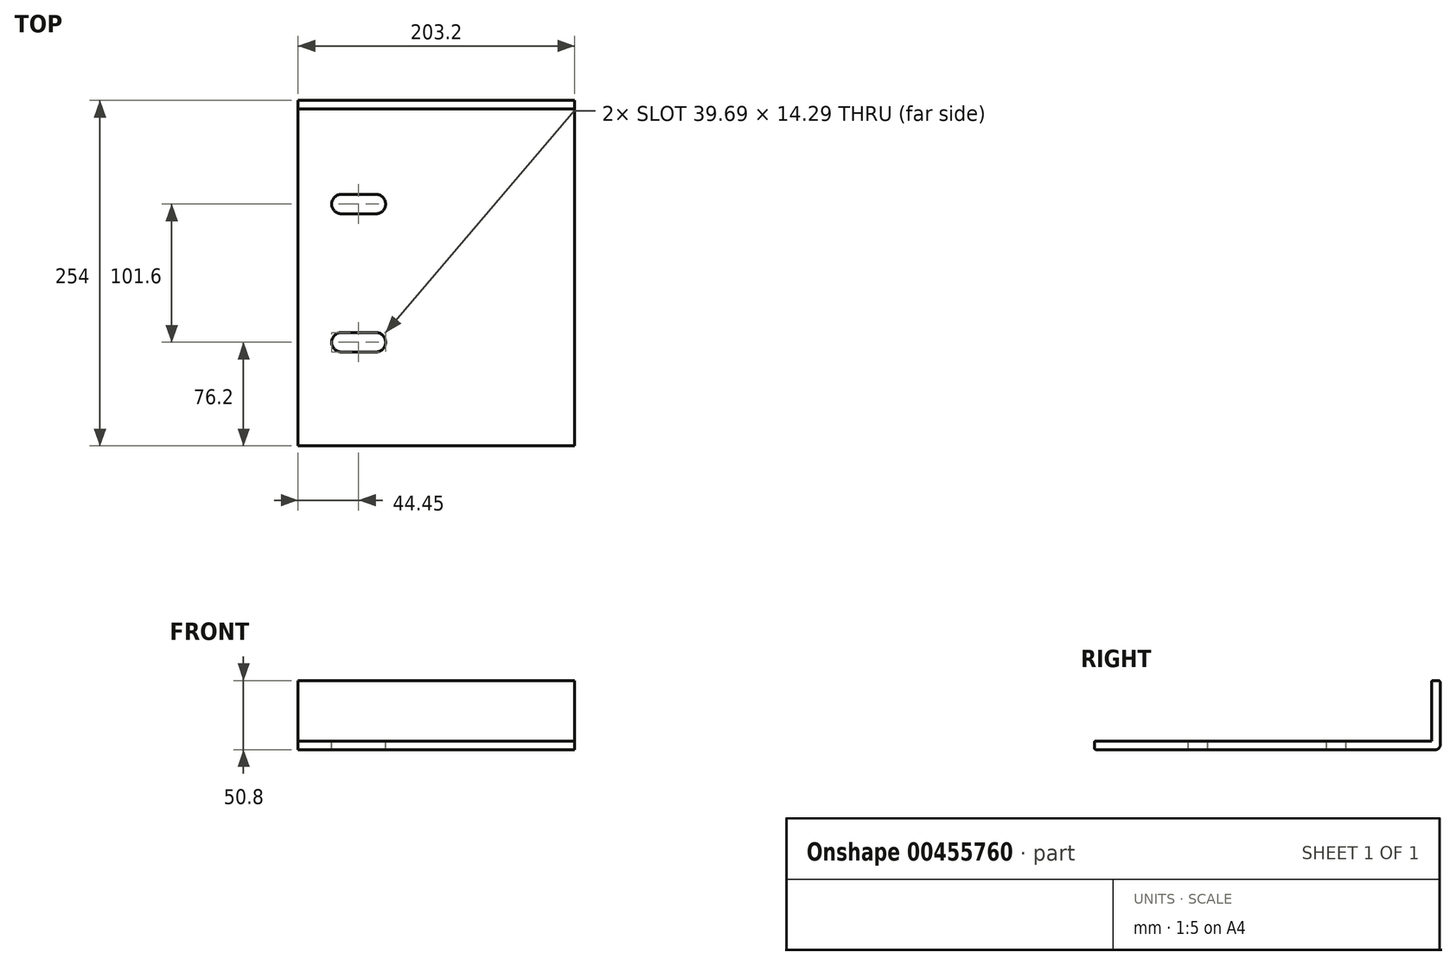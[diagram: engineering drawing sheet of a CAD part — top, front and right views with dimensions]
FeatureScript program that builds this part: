
annotation { "Feature Type Name" : "Feature", "Feature Type Description" : "" }
export const myFeature = defineFeature(function(context is Context, id is Id, definition is map)
    precondition{}
    {
        {
            var Q0;
            Q0=qCreatedBy(makeId("Top.planeOp"),FACE);
            var sketch = newSketch(context, id + "F0", { "sketchPlane" : qUnion([Q0])});
            skLineSegment(sketch, "E0.bottom", {"start": v(-101.6, -127) * mm, "end": v(101.6, -127) * mm});
            skLineSegment(sketch, "E0.top", {"start": v(-101.6, 127) * mm, "end": v(101.6, 127) * mm});
            skLineSegment(sketch, "E0.left", {"start": v(-101.6, -127) * mm, "end": v(-101.6, 127) * mm});
            skLineSegment(sketch, "E0.right", {"start": v(101.6, -127) * mm, "end": v(101.6, 127) * mm});
            skPoint(sketch, "E0.middle", {"position": v(0, 0) * mm});
            skSolve(sketch);
        }
        {
            var Q0;
            Q0 = qSketchRegion(id + "F0", true);
            extrude(context, id + "F1", {"entities" : qUnion([Q0]), "depth" : 6.35 * mm});
        }
        {
            var Q0;
            Q0=makeQuery(id+"F1.opExtrude","CAP_FACE",FACE,{"disambiguationData":[OSD([sQuery(id+"F0.wireOp",EDGE,"E0.bottom"),sQuery(id+"F0.wireOp",EDGE,"E0.top"),sQuery(id+"F0.wireOp",EDGE,"E0.left"),sQuery(id+"F0.wireOp",EDGE,"E0.right")])],"isStart":false});
            var sketch = newSketch(context, id + "F2", { "sketchPlane" : qUnion([Q0])});
            skLineSegment(sketch, "E1.bottom", {"start": v(-101.6, 127) * mm, "end": v(101.6, 127) * mm});
            skLineSegment(sketch, "E1.top", {"start": v(-101.6, 120.65) * mm, "end": v(101.6, 120.65) * mm});
            skLineSegment(sketch, "E1.left", {"start": v(-101.6, 127) * mm, "end": v(-101.6, 120.65) * mm});
            skLineSegment(sketch, "E1.right", {"start": v(101.6, 127) * mm, "end": v(101.6, 120.65) * mm});
            skSolve(sketch);
        }
        {
            var Q0;
            Q0 = qSketchRegion(id + "F2", true);
            extrude(context, id + "F3", {"entities" : qUnion([Q0]), "operationType" : NewBodyOperationType.ADD, "depth" : 44.45 * mm});
        }
        {
            var Q0;
            Q0=makeQuery(id+"F3.opExtrude","CAP_EDGE",EDGE,{"disambiguationData":[OSD([sQuery(id+"F2.wireOp",EDGE,"E1.top")])],"isStart":true});
            var Q1;
            Q1=makeQuery(id+"F1.opExtrude","CAP_EDGE",EDGE,{"disambiguationData":[OSD([sQuery(id+"F0.wireOp",EDGE,"E0.top")])],"isStart":true});
            fillet(context, id + "F4", {"entities" : qUnion([Q0, Q1]), "radius" : 3.17 * mm, "tangentPropagation" : true, "allowEdgeOverflow" : false});
        }
        {
            var Q0;
            Q0=makeQuery(id+"F1.opExtrude","CAP_FACE",FACE,{"disambiguationData":[OSD([sQuery(id+"F0.wireOp",EDGE,"E0.bottom"),sQuery(id+"F0.wireOp",EDGE,"E0.top"),sQuery(id+"F0.wireOp",EDGE,"E0.left"),sQuery(id+"F0.wireOp",EDGE,"E0.right")])],"isStart":false});
            var sketch = newSketch(context, id + "F5", { "sketchPlane" : qUnion([Q0])});
            skLineSegment(sketch, "E2", {"start": v(-101.6, -127) * mm, "end": v(-69.85, -127) * mm, "construction": true});
            skLineSegment(sketch, "E3", {"start": v(-69.85, -127) * mm, "end": v(-69.85, -50.8) * mm, "construction": true});
            skLineSegment(sketch, "E4", {"start": v(-69.85, -50.8) * mm, "end": v(-69.85, 50.8) * mm, "construction": true});
            skLineSegment(sketch, "E5", {"start": v(-69.85, 50.8) * mm, "end": v(-101.6, 50.8) * mm, "construction": true});
            skLineSegment(sketch, "E6", {"start": v(-69.85, -50.8) * mm, "end": v(-101.6, -50.8) * mm, "construction": true});
            skCircle(sketch, "E7", {"center": v(-69.85, -50.8) * mm, "radius": 7.14 * mm});
            skCircle(sketch, "E8", {"center": v(-69.85, 50.8) * mm, "radius": 7.14 * mm});
            skLineSegment(sketch, "E9", {"start": v(-69.85, 50.8) * mm, "end": v(-77, 50.8) * mm, "construction": true});
            skLineSegment(sketch, "E10", {"start": v(-69.85, 50.8) * mm, "end": v(-44.45, 50.8) * mm, "construction": true});
            skLineSegment(sketch, "E11", {"start": v(-69.85, -50.8) * mm, "end": v(-44.45, -50.8) * mm, "construction": true});
            skCircle(sketch, "E12", {"center": v(-44.45, -50.8) * mm, "radius": 7.14 * mm});
            skCircle(sketch, "E13", {"center": v(-44.45, 50.8) * mm, "radius": 7.14 * mm});
            skLineSegment(sketch, "E14", {"start": v(-69.85, -57.94) * mm, "end": v(-44.45, -57.94) * mm});
            skLineSegment(sketch, "E15", {"start": v(-69.85, -43.66) * mm, "end": v(-44.45, -43.66) * mm});
            skLineSegment(sketch, "E16", {"start": v(-69.85, 43.66) * mm, "end": v(-44.45, 43.66) * mm});
            skLineSegment(sketch, "E17", {"start": v(-69.85, 57.94) * mm, "end": v(-44.45, 57.94) * mm});
            skSolve(sketch);
        }
        {
            var Q0;
            {var subQ0=sQuery(id+"F5.wireOp",EDGE,"E14");Q0=makeQuery(id+"F5.imprint","IMPRINT",FACE,{"disambiguationData":[TD([[makeQuery(id+"F5.imprint","IMPRINT",EDGE,{"derivedFrom":subQ0}),1.0]])]});}
            var Q1;
            {var subQ0=sQuery(id+"F5.wireOp",EDGE,"E12");var subQ1=makeQuery(id+"F5.imprint","INTERSECT",VERTEX,{"derivedFrom":[subQ0,sQuery(id+"F5.wireOp",EDGE,"E14")]});Q1=makeQuery(id+"F5.imprint","IMPRINT",FACE,{"disambiguationData":[TD([[makeQuery(id+"F5.imprint","IMPRINT",EDGE,{"disambiguationData":[TD([[subQ1,1.0]])],"derivedFrom":subQ0}),1.0]])]});}
            var Q2;
            {var subQ0=sQuery(id+"F5.wireOp",EDGE,"E7");var subQ1=makeQuery(id+"F5.imprint","INTERSECT",VERTEX,{"derivedFrom":[subQ0,sQuery(id+"F5.wireOp",EDGE,"E14")]});Q2=makeQuery(id+"F5.imprint","IMPRINT",FACE,{"disambiguationData":[TD([[makeQuery(id+"F5.imprint","IMPRINT",EDGE,{"disambiguationData":[TD([[subQ1,1.0]])],"derivedFrom":subQ0}),1.0]])]});}
            extrude(context, id + "F6", {"entities" : qUnion([Q0, Q1, Q2]), "operationType" : NewBodyOperationType.REMOVE, "oppositeDirection" : true, "depth" : 25.4 * mm});
        }
        {
            var Q0;
            Q0 = qSketchRegion(id + "F5", true);
            extrude(context, id + "F7", {"entities" : qUnion([Q0]), "operationType" : NewBodyOperationType.REMOVE, "oppositeDirection" : true, "depth" : 25.4 * mm});
        }
        {
            var Q0;
            Q0=makeQuery(id+"F1.opExtrude","CAP_EDGE",EDGE,{"disambiguationData":[OSD([sQuery(id+"F0.wireOp",EDGE,"E0.bottom")])],"isStart":false});
            var Q1;
            Q1=makeQuery(id+"F1.opExtrude","CAP_EDGE",EDGE,{"disambiguationData":[OSD([sQuery(id+"F0.wireOp",EDGE,"E0.bottom")])],"isStart":true});
            var Q2;
            Q2=makeQuery(id+"F3.opExtrude","CAP_EDGE",EDGE,{"disambiguationData":[OSD([sQuery(id+"F2.wireOp",EDGE,"E1.top")])],"isStart":false});
            var Q3;
            Q3=makeQuery(id+"F3.opExtrude","CAP_EDGE",EDGE,{"disambiguationData":[OSD([sQuery(id+"F2.wireOp",EDGE,"E1.bottom")])],"isStart":false});
            fillet(context, id + "F8", {"entities" : qUnion([Q0, Q1, Q2, Q3]), "radius" : 1.27 * mm, "tangentPropagation" : true, "allowEdgeOverflow" : false});
        }
    });
